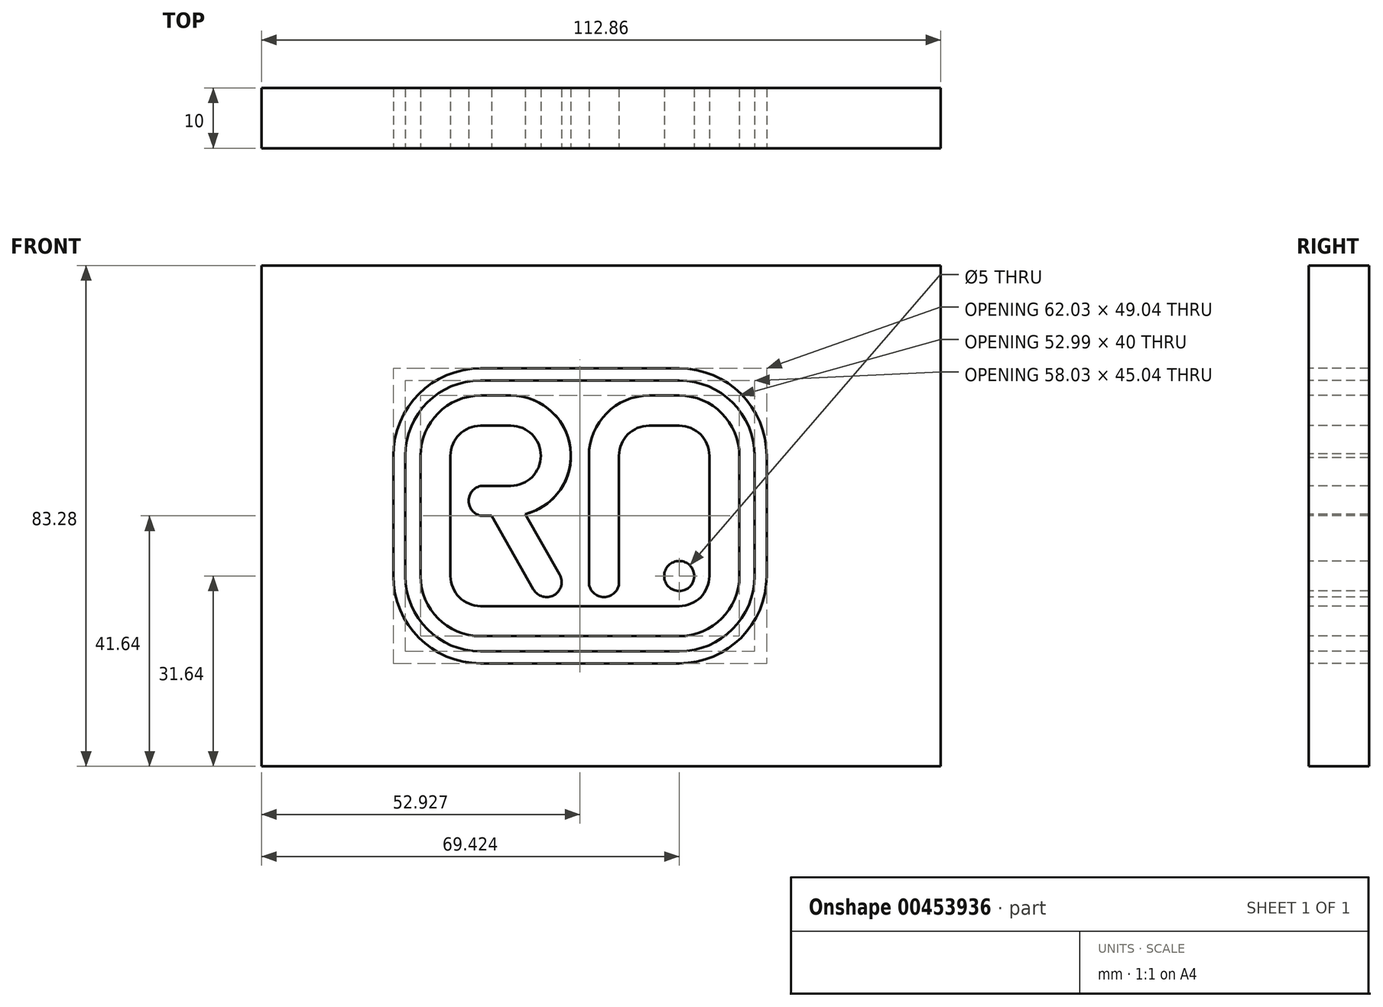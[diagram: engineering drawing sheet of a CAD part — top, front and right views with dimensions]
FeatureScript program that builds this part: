
annotation { "Feature Type Name" : "Feature", "Feature Type Description" : "" }
export const myFeature = defineFeature(function(context is Context, id is Id, definition is map)
    precondition{}
    {
        {
            var Q0;
            Q0=qCreatedBy(makeId("Front.planeOp"),FACE);
            var sketch = newSketch(context, id + "F0", { "sketchPlane" : qUnion([Q0])});
            skPoint(sketch, "E0.middle", {"position": v(0, 0) * mm});
            skLineSegment(sketch, "E1", {"start": v(-25, 10) * mm, "end": v(-25, -10) * mm});
            skLineSegment(sketch, "E2", {"start": v(-2, -20) * mm, "end": v(-0.38, -20) * mm});
            skLineSegment(sketch, "E3", {"start": v(-2, -11) * mm, "end": v(-2, 10) * mm});
            skLineSegment(sketch, "E4", {"start": v(8, 20) * mm, "end": v(13, 20) * mm});
            skLineSegment(sketch, "E5", {"start": v(23, 10) * mm, "end": v(23, -10) * mm});
            skLineSegment(sketch, "E6", {"start": v(13, -20) * mm, "end": v(9, -20) * mm});
            skLineSegment(sketch, "E7", {"start": v(-25, 20) * mm, "end": v(-15, 20) * mm});
            skLineSegment(sketch, "E8", {"start": v(-19.5, 0) * mm, "end": v(-15, 0) * mm});
            skLineSegment(sketch, "E9", {"start": v(-5, 10.33) * mm, "end": v(-5, 10.33) * mm});
            skPoint(sketch, "E10.visualSharp", {"position": v(-5.33, 20) * mm});
            skArc(sketch, "E10.filletArc", {"start": v(-5, 10.33) * mm, "mid": v(-8.05, 17.19) * mm, "end": v(-15, 20) * mm});
            skArc(sketch, "E11.filletArc", {"start": v(-15, 0) * mm, "mid": v(-7.81, 3.05) * mm, "end": v(-5, 10.33) * mm});
            skPoint(sketch, "E12.visualSharp", {"position": v(-3.63, -20) * mm});
            skPoint(sketch, "E13.visualSharp", {"position": v(23, -20) * mm});
            skArc(sketch, "E13.filletArc", {"start": v(13, -20) * mm, "mid": v(20.07, -17.07) * mm, "end": v(23, -10) * mm});
            skPoint(sketch, "E14.visualSharp", {"position": v(23, 20) * mm});
            skArc(sketch, "E14.filletArc", {"start": v(23, 10) * mm, "mid": v(20.07, 17.07) * mm, "end": v(13, 20) * mm});
            skPoint(sketch, "E15.visualSharp", {"position": v(-2, 20) * mm});
            skArc(sketch, "E15.filletArc", {"start": v(8, 20) * mm, "mid": v(0.92, 17.07) * mm, "end": v(-2, 10) * mm});
            skPoint(sketch, "E16.visualSharp", {"position": v(-2, -20) * mm});
            skArc(sketch, "E17.0", {"start": v(8, 15) * mm, "mid": v(4.46, 13.54) * mm, "end": v(3, 10) * mm});
            skLineSegment(sketch, "E17.1", {"start": v(3, -11) * mm, "end": v(3, 10) * mm});
            skLineSegment(sketch, "E17.2", {"start": v(8, 15) * mm, "end": v(13, 15) * mm});
            skArc(sketch, "E17.4", {"start": v(18, 10) * mm, "mid": v(16.53, 13.54) * mm, "end": v(13, 15) * mm});
            skLineSegment(sketch, "E17.5", {"start": v(18, 10) * mm, "end": v(18, -10) * mm});
            skArc(sketch, "E17.6", {"start": v(13, -15) * mm, "mid": v(16.53, -13.54) * mm, "end": v(18, -10) * mm});
            skLineSegment(sketch, "E17.7", {"start": v(13, -15) * mm, "end": v(9, -15) * mm});
            skArc(sketch, "E18.1", {"start": v(-15, 5) * mm, "mid": v(-11.44, 6.5) * mm, "end": v(-10, 10.08) * mm});
            skArc(sketch, "E18.2", {"start": v(-10, 10.08) * mm, "mid": v(-11.5, 13.56) * mm, "end": v(-15, 15) * mm});
            skLineSegment(sketch, "E18.3", {"start": v(-20, 15) * mm, "end": v(-15, 15) * mm});
            skLineSegment(sketch, "E19.0", {"start": v(-30, 17.5) * mm, "end": v(-30, -10) * mm});
            skLineSegment(sketch, "E20.0", {"start": v(-1, -15) * mm, "end": v(-0.38, -15) * mm});
            skLineSegment(sketch, "E21", {"start": v(-20, -20) * mm, "end": v(-2, -20) * mm});
            skLineSegment(sketch, "E22", {"start": v(-1, -15) * mm, "end": v(9, -15) * mm});
            skLineSegment(sketch, "E23.0", {"start": v(-20, -15) * mm, "end": v(0, -15) * mm});
            skLineSegment(sketch, "E24", {"start": v(-5, 10.33) * mm, "end": v(-5, 0) * mm});
            skLineSegment(sketch, "E25", {"start": v(0.5, -13.5) * mm, "end": v(0.5, -13.5) * mm});
            skPoint(sketch, "E26.visualSharp", {"position": v(3, -13.5) * mm});
            skArc(sketch, "E26.filletArc", {"start": v(0.5, -13.5) * mm, "mid": v(2.26, -12.77) * mm, "end": v(3, -11) * mm});
            skPoint(sketch, "E27.newPointB", {"position": v(-23.5, -13.5) * mm});
            skArc(sketch, "E27.filletArc", {"start": v(-2, -11) * mm, "mid": v(-1.27, -12.77) * mm, "end": v(0.5, -13.5) * mm});
            skPoint(sketch, "E28.visualSharp", {"position": v(-30, -20) * mm});
            skArc(sketch, "E28.filletArc", {"start": v(-30, -19.5) * mm, "mid": v(-29.85, -19.85) * mm, "end": v(-29.5, -20) * mm});
            skLineSegment(sketch, "E29", {"start": v(-7.28, -12.77) * mm, "end": v(-7.28, -12.77) * mm});
            skArc(sketch, "E30.filletArc", {"start": v(-7.28, -12.77) * mm, "mid": v(-6.55, -11) * mm, "end": v(-7.27, -9.24) * mm});
            skArc(sketch, "E31.filletArc", {"start": v(-11.23, -12.21) * mm, "mid": v(-9.4, -13.48) * mm, "end": v(-7.28, -12.77) * mm});
            skLineSegment(sketch, "E32.0", {"start": v(14.76, -15.3) * mm, "end": v(14.29, -14.83) * mm});
            skPoint(sketch, "E33.newPointB", {"position": v(-25, 20) * mm});
            skPoint(sketch, "E34.visualSharp", {"position": v(-23.5, 5) * mm});
            skPoint(sketch, "E35.visualSharp", {"position": v(-23.5, 0) * mm});
            skLineSegment(sketch, "E36", {"start": v(-30, 10) * mm, "end": v(-30, 17.5) * mm});
            skLineSegment(sketch, "E37", {"start": v(-20, 20) * mm, "end": v(-25, 20) * mm});
            skPoint(sketch, "E38.visualSharp", {"position": v(-30, 20) * mm});
            skArc(sketch, "E38.filletArc", {"start": v(-20, 20) * mm, "mid": v(-27.07, 17.07) * mm, "end": v(-30, 10) * mm});
            skPoint(sketch, "E39", {"position": v(20.07, -17.07) * mm});
            skPoint(sketch, "E40.orphan", {"position": v(16.53, -13.54) * mm});
            skLineSegment(sketch, "E41.trimOffspring", {"start": v(13, -20) * mm, "end": v(-0.38, -20) * mm});
            skPoint(sketch, "E42.newPointB", {"position": v(-25, -20) * mm});
            skArc(sketch, "E42.filletArc", {"start": v(-25, -10) * mm, "mid": v(-23.54, -13.54) * mm, "end": v(-20, -15) * mm});
            skLineSegment(sketch, "E43", {"start": v(-15, 20) * mm, "end": v(8, 20) * mm});
            skLineSegment(sketch, "E44", {"start": v(21.86, -24.52) * mm, "end": v(-20, -24.52) * mm});
            skLineSegment(sketch, "E45", {"start": v(27.51, -22.02) * mm, "end": v(27.51, -18.86) * mm});
            skLineSegment(sketch, "E46", {"start": v(13, 24.52) * mm, "end": v(-20, 24.52) * mm});
            skLineSegment(sketch, "E47", {"start": v(-34.52, -10) * mm, "end": v(-34.52, 10) * mm});
            skPoint(sketch, "E48.orphan", {"position": v(17.43, -17.97) * mm});
            skPoint(sketch, "E49.orphan", {"position": v(13.35, -13.89) * mm});
            skArc(sketch, "E50.0", {"start": v(27.51, 10) * mm, "mid": v(23.26, 20.27) * mm, "end": v(13, 24.52) * mm});
            skArc(sketch, "E51.0", {"start": v(25.51, 10) * mm, "mid": v(21.85, 18.85) * mm, "end": v(13, 22.52) * mm});
            skLineSegment(sketch, "E52.0", {"start": v(25.51, -22.07) * mm, "end": v(25.51, -18.99) * mm});
            skLineSegment(sketch, "E53.0", {"start": v(25.02, -22.52) * mm, "end": v(21.98, -22.52) * mm});
            skLineSegment(sketch, "E54.0", {"start": v(-32.52, -10) * mm, "end": v(-32.52, 10) * mm});
            skLineSegment(sketch, "E55.0", {"start": v(13, 22.52) * mm, "end": v(-20, 22.52) * mm});
            skPoint(sketch, "E56.visualSharp", {"position": v(-32.52, 22.52) * mm});
            skArc(sketch, "E56.filletArc", {"start": v(-20, 22.52) * mm, "mid": v(-28.85, 18.85) * mm, "end": v(-32.52, 10) * mm});
            skArc(sketch, "E57.0", {"start": v(-20, 24.52) * mm, "mid": v(-30.27, 20.27) * mm, "end": v(-34.52, 10) * mm});
            skPoint(sketch, "E58.visualSharp", {"position": v(-32.52, -22.52) * mm});
            skLineSegment(sketch, "E59", {"start": v(26.51, -15) * mm, "end": v(26.51, -16.32) * mm});
            skLineSegment(sketch, "E60.0", {"start": v(18.1, -20.77) * mm, "end": v(22.19, -24.85) * mm, "construction": true});
            skLineSegment(sketch, "E61.0", {"start": v(23.76, -15.1) * mm, "end": v(27.84, -19.2) * mm, "construction": true});
            skLineSegment(sketch, "E62.trimOffspring", {"start": v(25.51, -14) * mm, "end": v(25.51, 10) * mm});
            skLineSegment(sketch, "E63.trimOffspring", {"start": v(27.51, -14) * mm, "end": v(27.51, 33) * mm});
            skLineSegment(sketch, "E64.trimOffspring", {"start": v(19.86, -22.52) * mm, "end": v(-20, -22.52) * mm});
            skLineSegment(sketch, "E65", {"start": v(21.86, -24.52) * mm, "end": v(25.02, -24.52) * mm});
            skLineSegment(sketch, "E66", {"start": v(27.51, -14) * mm, "end": v(27.51, -22.02) * mm});
            skLineSegment(sketch, "E67.bottom", {"start": v(-56.43, 41.64) * mm, "end": v(56.43, 41.64) * mm});
            skLineSegment(sketch, "E67.top", {"start": v(-56.43, -41.64) * mm, "end": v(56.43, -41.64) * mm});
            skLineSegment(sketch, "E67.left", {"start": v(-56.43, 41.64) * mm, "end": v(-56.43, -41.64) * mm});
            skLineSegment(sketch, "E67.right", {"start": v(56.43, 41.64) * mm, "end": v(56.43, -41.64) * mm});
            skLineSegment(sketch, "E68", {"start": v(0, 0) * mm, "end": v(0, -38.7) * mm, "construction": true});
            skLineSegment(sketch, "E69", {"start": v(0, 0) * mm, "end": v(33.56, 0) * mm, "construction": true});
            skArc(sketch, "E70.filletArc", {"start": v(-20, 15) * mm, "mid": v(-23.54, 13.54) * mm, "end": v(-25, 10) * mm});
            skArc(sketch, "E71.0", {"start": v(-30, -10) * mm, "mid": v(-27.07, -17.07) * mm, "end": v(-20, -20) * mm});
            skArc(sketch, "E72.0", {"start": v(-34.52, -10) * mm, "mid": v(-30.27, -20.27) * mm, "end": v(-20, -24.52) * mm});
            skArc(sketch, "E73.0", {"start": v(-32.52, -10) * mm, "mid": v(-28.85, -18.85) * mm, "end": v(-20, -22.52) * mm});
            skLineSegment(sketch, "E74", {"start": v(-15, 5) * mm, "end": v(-19.5, 5) * mm});
            skLineSegment(sketch, "E75", {"start": v(-23.5, 2.5) * mm, "end": v(-23.5, 2.5) * mm});
            skArc(sketch, "E76.filletArc", {"start": v(-21, 5) * mm, "mid": v(-22.77, 4.27) * mm, "end": v(-23.5, 2.5) * mm, "construction": true});
            skArc(sketch, "E77.filletArc", {"start": v(-23.5, 2.5) * mm, "mid": v(-22.77, 0.73) * mm, "end": v(-21, 0) * mm, "construction": true});
            skPoint(sketch, "E78.startSnap0", {"position": v(-6.55, -11) * mm});
            skLineSegment(sketch, "E79", {"start": v(-22.87, 0.84) * mm, "end": v(-10.92, -12.66) * mm, "construction": true});
            skLineSegment(sketch, "E80.0", {"start": v(-19.13, 4.16) * mm, "end": v(-7.17, -9.34) * mm, "construction": true});
            skArc(sketch, "E81.0", {"start": v(13, -22.52) * mm, "mid": v(21.85, -18.85) * mm, "end": v(25.51, -10) * mm});
            skArc(sketch, "E82.0", {"start": v(13, -24.52) * mm, "mid": v(23.26, -20.27) * mm, "end": v(27.51, -10) * mm});
            skCircle(sketch, "E83", {"center": v(13, -10) * mm, "radius": 2.5 * mm});
            skLineSegment(sketch, "E84", {"start": v(-21, 5) * mm, "end": v(-21, 0) * mm, "construction": true});
            skLineSegment(sketch, "E85", {"start": v(-21, 5) * mm, "end": v(-11.1, -12.46) * mm});
            skLineSegment(sketch, "E86.0", {"start": v(-16.65, 7.47) * mm, "end": v(-6.74, -10) * mm});
            skLineSegment(sketch, "E87", {"start": v(-22, 7.3) * mm, "end": v(-22, -4.59) * mm});
            skLineSegment(sketch, "E88", {"start": v(-28.56, 2.5) * mm, "end": v(-6.16, 2.5) * mm, "construction": true});
            skCircle(sketch, "E89", {"center": v(-19.5, 2.5) * mm, "radius": 2.5 * mm});
            skSolve(sketch);
        }
        {
            var Q0;
            Q0=makeQuery(id+"F0.imprint","IMPRINT",FACE,{"disambiguationData":[TD([[makeQuery(id+"F0.imprint","IMPRINT",EDGE,{"derivedFrom":sQuery(id+"F0.wireOp",EDGE,"E1")}),-1.0]])]});
            var Q1;
            {var subQ6=sQuery(id+"F0.wireOp",EDGE,"8dgEX87s-OnN3-UPAw-RyUf-tcfM0RuKeMZf");Q1=makeQuery(id+"F0.imprint","IMPRINT",FACE,{"disambiguationData":[TD([[makeQuery(id+"F0.imprint","IMPRINT",EDGE,{"derivedFrom":subQ6}),1.0]])]});}
            var Q2;
            {var subQ0=sQuery(id+"F0.wireOp",EDGE,"S70SFG3v-wlmV-iE8w-7gkR-MiBzXbBwRlH9");var subQ1=makeQuery(id+"F0.imprint","INTERSECT",VERTEX,{"derivedFrom":[sQuery(id+"F0.wireOp",EDGE,"c0c087a9-fd36-4214-a694-875f0f01d769.0"),subQ0]});Q2=makeQuery(id+"F0.imprint","IMPRINT",FACE,{"disambiguationData":[TD([[makeQuery(id+"F0.imprint","IMPRINT",EDGE,{"disambiguationData":[TD([[subQ1,-1.0]])],"derivedFrom":subQ0}),1.0]])]});}
            var Q3;
            {var subQ1=sQuery(id+"F0.wireOp",EDGE,"c0c087a9-fd36-4214-a694-875f0f01d769.0");Q3=makeQuery(id+"F0.imprint","IMPRINT",FACE,{"disambiguationData":[TD([[makeQuery(id+"F0.imprint","IMPRINT",EDGE,{"derivedFrom":subQ1}),-1.0]])]});}
            var Q4;
            {var subQ0=sQuery(id+"F0.wireOp",EDGE,"E0.bottom");Q4=makeQuery(id+"F0.imprint","IMPRINT",FACE,{"disambiguationData":[TD([[makeQuery(id+"F0.imprint","IMPRINT",EDGE,{"derivedFrom":subQ0}),-1.0]])]});}
            var Q5;
            {var subQ0=sQuery(id+"F0.wireOp",EDGE,"E0.bottom");Q5=makeQuery(id+"F0.imprint","IMPRINT",FACE,{"disambiguationData":[TD([[makeQuery(id+"F0.imprint","IMPRINT",EDGE,{"derivedFrom":subQ0}),1.0]])]});}
            var Q6;
            {var subQ3=sQuery(id+"F0.wireOp",EDGE,"E8");var subQ7=sQuery(id+"F0.wireOp",EDGE,"E11.filletArc");var subQ8=makeQuery(id+"F0.imprint","INTERSECT",VERTEX,{"derivedFrom":[subQ3,subQ7]});Q6=makeQuery(id+"F0.imprint","IMPRINT",FACE,{"disambiguationData":[TD([[makeQuery(id+"F0.imprint","IMPRINT",EDGE,{"disambiguationData":[TD([[subQ8,1.0]])],"derivedFrom":subQ3}),1.0]])]});}
            var Q7;
            {var subQ4=sQuery(id+"F0.wireOp",EDGE,"E76.filletArc");Q7=makeQuery(id+"F0.imprint","IMPRINT",FACE,{"disambiguationData":[TD([[makeQuery(id+"F0.imprint","IMPRINT",EDGE,{"derivedFrom":subQ4}),1.0]])]});}
            var Q8;
            {var subQ0=sQuery(id+"F0.wireOp",EDGE,"E31.filletArc");Q8=makeQuery(id+"F0.imprint","IMPRINT",FACE,{"disambiguationData":[TD([[makeQuery(id+"F0.imprint","IMPRINT",EDGE,{"derivedFrom":subQ0}),1.0]])]});}
            var Q9;
            Q9=makeQuery(id+"F0.imprint","IMPRINT",FACE,{"disambiguationData":[TD([[makeQuery(id+"F0.imprint","IMPRINT",EDGE,{"derivedFrom":sQuery(id+"F0.wireOp",EDGE,"E83")}),1.0]])]});
            var Q10;
            {var subQ0=sQuery(id+"F0.wireOp",EDGE,"E88");var subQ1=sQuery(id+"F0.wireOp",EDGE,"E11.filletArc");var subQ2=makeQuery(id+"F0.imprint","INTERSECT",VERTEX,{"derivedFrom":[subQ1,subQ0]});Q10=makeQuery(id+"F0.imprint","IMPRINT",FACE,{"disambiguationData":[TD([[makeQuery(id+"F0.imprint","IMPRINT",EDGE,{"disambiguationData":[TD([[subQ2,1.0]])],"derivedFrom":subQ1}),1.0]])]});}
            var Q11;
            {var subQ0=sQuery(id+"F0.wireOp",EDGE,"E89");var subQ1=sQuery(id+"F0.wireOp",EDGE,"E74");var subQ2=makeQuery(id+"F0.imprint","INTERSECT",VERTEX,{"derivedFrom":[subQ1,subQ0]});Q11=makeQuery(id+"F0.imprint","IMPRINT",FACE,{"disambiguationData":[TD([[makeQuery(id+"F0.imprint","IMPRINT",EDGE,{"disambiguationData":[TD([[subQ2,1.0]])],"derivedFrom":subQ1}),1.0]])]});}
            var Q12;
            {var subQ0=sQuery(id+"F0.wireOp",EDGE,"E88");var subQ1=sQuery(id+"F0.wireOp",EDGE,"E85");var subQ2=makeQuery(id+"F0.imprint","INTERSECT",VERTEX,{"derivedFrom":[subQ1,subQ0]});Q12=makeQuery(id+"F0.imprint","IMPRINT",FACE,{"disambiguationData":[TD([[makeQuery(id+"F0.imprint","IMPRINT",EDGE,{"disambiguationData":[TD([[subQ2,-1.0]])],"derivedFrom":subQ1}),-1.0]])]});}
            var Q13;
            {var subQ0=sQuery(id+"F0.wireOp",EDGE,"E89");var subQ1=sQuery(id+"F0.wireOp",EDGE,"E85");var subQ2=makeQuery(id+"F0.imprint","INTERSECT",VERTEX,{"disambiguationData":[OD(0.0)],"derivedFrom":[subQ1,subQ0]});Q13=makeQuery(id+"F0.imprint","IMPRINT",FACE,{"disambiguationData":[TD([[makeQuery(id+"F0.imprint","IMPRINT",EDGE,{"disambiguationData":[TD([[subQ2,-1.0]])],"derivedFrom":subQ1}),-1.0]])]});}
            var Q14;
            {var subQ0=sQuery(id+"F0.wireOp",EDGE,"E89");var subQ1=sQuery(id+"F0.wireOp",EDGE,"E85");var subQ2=makeQuery(id+"F0.imprint","INTERSECT",VERTEX,{"disambiguationData":[OD(0.0)],"derivedFrom":[subQ1,subQ0]});Q14=makeQuery(id+"F0.imprint","IMPRINT",FACE,{"disambiguationData":[TD([[makeQuery(id+"F0.imprint","IMPRINT",EDGE,{"disambiguationData":[TD([[subQ2,-1.0]])],"derivedFrom":subQ1}),1.0]])]});}
            var Q15;
            {var subQ0=sQuery(id+"F0.wireOp",EDGE,"E88");var subQ1=sQuery(id+"F0.wireOp",EDGE,"E85");var subQ2=makeQuery(id+"F0.imprint","INTERSECT",VERTEX,{"derivedFrom":[subQ1,subQ0]});Q15=makeQuery(id+"F0.imprint","IMPRINT",FACE,{"disambiguationData":[TD([[makeQuery(id+"F0.imprint","IMPRINT",EDGE,{"disambiguationData":[TD([[subQ2,-1.0]])],"derivedFrom":subQ1}),1.0]])]});}
            var Q16;
            {var subQ0=sQuery(id+"F0.wireOp",EDGE,"E89");var subQ1=sQuery(id+"F0.wireOp",EDGE,"E8");var subQ2=makeQuery(id+"F0.imprint","INTERSECT",VERTEX,{"derivedFrom":[subQ1,subQ0]});Q16=makeQuery(id+"F0.imprint","IMPRINT",FACE,{"disambiguationData":[TD([[makeQuery(id+"F0.imprint","IMPRINT",EDGE,{"disambiguationData":[TD([[subQ2,-1.0]])],"derivedFrom":subQ1}),1.0]])]});}
            extrude(context, id + "F1", {"entities" : qUnion([Q0, Q1, Q2, Q3, Q4, Q5, Q6, Q7, Q8, Q9, Q10, Q11, Q12, Q13, Q14, Q15, Q16]), "oppositeDirection" : true, "depth" : 10 * mm});
        }
        {
            var Q0;
            Q0=makeQuery(id+"F0.imprint","IMPRINT",FACE,{"disambiguationData":[TD([[makeQuery(id+"F0.imprint","IMPRINT",EDGE,{"derivedFrom":sQuery(id+"F0.wireOp",EDGE,"E1")}),1.0]])]});
            var Q1;
            {var subQ16=sQuery(id+"F0.wireOp",EDGE,"E2");Q1=makeQuery(id+"F0.imprint","IMPRINT",FACE,{"disambiguationData":[TD([[makeQuery(id+"F0.imprint","IMPRINT",EDGE,{"derivedFrom":subQ16}),-1.0]])]});}
            extrude(context, id + "F2", {"entities" : qUnion([Q0, Q1]), "oppositeDirection" : true, "depth" : 10 * mm});
        }
        {
            var Q0;
            Q0=makeQuery(id+"F0.imprint","IMPRINT",FACE,{"disambiguationData":[TD([[makeQuery(id+"F0.imprint","IMPRINT",EDGE,{"derivedFrom":sQuery(id+"F0.wireOp",EDGE,"E46")}),1.0]])]});
            var Q1;
            {var subQ0=sQuery(id+"F0.wireOp",EDGE,"aTrX08yB-o83u-csdW-HvKf-6qn933KxLSEO");var subQ2=makeQuery(id+"F0.imprint","IMPRINT",VERTEX,{"derivedFrom":subQ0});Q1=makeQuery(id+"F0.imprint","IMPRINT",FACE,{"disambiguationData":[TD([[makeQuery(id+"F0.imprint","IMPRINT",EDGE,{"disambiguationData":[TD([[subQ2,-1.0]])],"derivedFrom":subQ0}),1.0]])]});}
            var Q2;
            {var subQ0=sQuery(id+"F0.wireOp",EDGE,"orb3SBHr-i0Mj-h6B2-otKM-5Ab6eh35dINg");var subQ3=makeQuery(id+"F0.imprint","IMPRINT",VERTEX,{"derivedFrom":subQ0});Q2=makeQuery(id+"F0.imprint","IMPRINT",FACE,{"disambiguationData":[TD([[makeQuery(id+"F0.imprint","IMPRINT",EDGE,{"disambiguationData":[TD([[subQ3,1.0]])],"derivedFrom":subQ0}),1.0]])]});}
            extrude(context, id + "F3", {"entities" : qUnion([Q0, Q1, Q2]), "oppositeDirection" : true, "depth" : 10 * mm});
        }
        {
            var Q0;
            Q0=makeQuery(id+"F0.imprint","IMPRINT",FACE,{"disambiguationData":[TD([[makeQuery(id+"F0.imprint","IMPRINT",EDGE,{"derivedFrom":sQuery(id+"F0.wireOp",EDGE,"E46")}),-1.0]])]});
            extrude(context, id + "F4", {"entities" : qUnion([Q0]), "oppositeDirection" : true, "depth" : 10 * mm});
        }
    });
